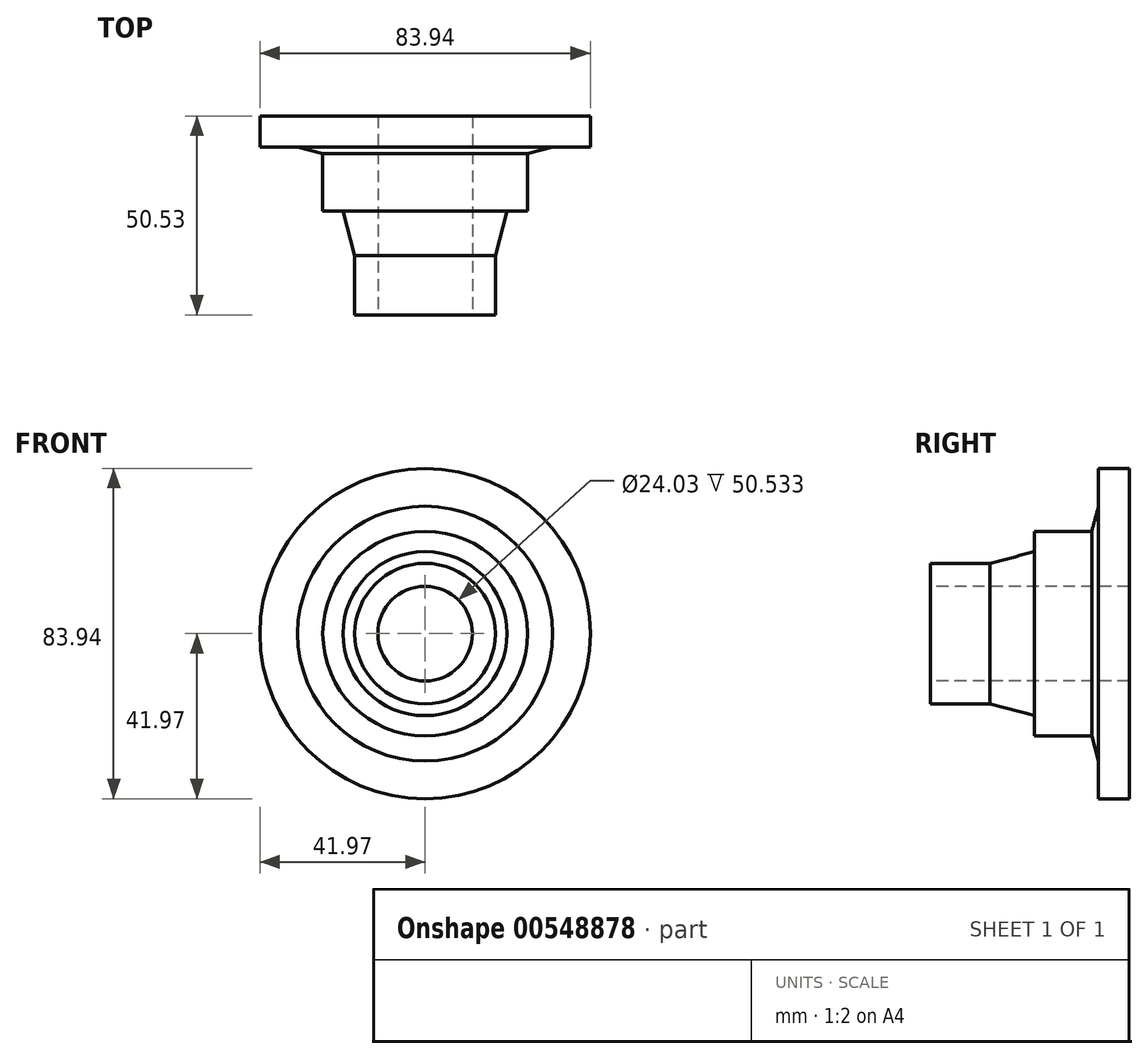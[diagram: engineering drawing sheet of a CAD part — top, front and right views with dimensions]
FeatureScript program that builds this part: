
annotation { "Feature Type Name" : "Feature", "Feature Type Description" : "" }
export const myFeature = defineFeature(function(context is Context, id is Id, definition is map)
    precondition{}
    {
        {
            var Q0;
            Q0=qCreatedBy(makeId("Right.planeOp"),FACE);
            var sketch = newSketch(context, id + "F0", { "sketchPlane" : qUnion([Q0])});
            skLineSegment(sketch, "E0", {"start": v(0, 0) * mm, "end": v(-50.53, 0) * mm});
            skLineSegment(sketch, "E1", {"start": v(-50.53, 0) * mm, "end": v(-50.53, 11.18) * mm});
            skLineSegment(sketch, "E2", {"start": v(-50.53, 11.18) * mm, "end": v(0, 11.18) * mm});
            skLineSegment(sketch, "E3", {"start": v(0, 11.18) * mm, "end": v(0, 0) * mm});
            skLineSegment(sketch, "E4", {"start": v(-50.53, 11.18) * mm, "end": v(-50.53, 17.86) * mm});
            skLineSegment(sketch, "E5", {"start": v(-50.53, 17.86) * mm, "end": v(-35.43, 17.86) * mm});
            skLineSegment(sketch, "E6", {"start": v(-35.43, 17.86) * mm, "end": v(-24.1, 20.84) * mm});
            skLineSegment(sketch, "E7", {"start": v(-24.1, 20.84) * mm, "end": v(-24.1, 26) * mm});
            skLineSegment(sketch, "E8", {"start": v(-24.1, 26) * mm, "end": v(-9.58, 26) * mm});
            skLineSegment(sketch, "E9", {"start": v(-9.58, 26) * mm, "end": v(-7.84, 32.38) * mm});
            skLineSegment(sketch, "E10", {"start": v(-7.84, 32.38) * mm, "end": v(-7.84, 41.97) * mm});
            skLineSegment(sketch, "E11", {"start": v(-7.84, 41.97) * mm, "end": v(0, 41.97) * mm});
            skLineSegment(sketch, "E12", {"start": v(0, 41.97) * mm, "end": v(0, 11.18) * mm});
            skSolve(sketch);
        }
        {
            var Q0;
            Q0=makeQuery(id+"F0.imprint","IMPRINT",FACE,{"disambiguationData":[TD([[makeQuery(id+"F0.imprint","IMPRINT",EDGE,{"derivedFrom":sQuery(id+"F0.wireOp",EDGE,"E2")}),1.0]])]});
            var Q1;
            Q1=makeQuery(id+"F0.imprint","IMPRINT",FACE,{"disambiguationData":[TD([[makeQuery(id+"F0.imprint","IMPRINT",EDGE,{"derivedFrom":sQuery(id+"F0.wireOp",EDGE,"E0")}),-1.0]])]});
            var Q2;
            Q2=sQuery(id+"F0.wireOp",EDGE,"E0");
            revolve(context, id + "F1", {"entities" : qUnion([Q0, Q1]), "axis" : qUnion([Q2]), "revolveType" : RevolveType.FULL});
        }
        {
            var Q0;
            Q0=makeQuery(id+"F1.opRevolve","SWEPT_FACE",FACE,{"disambiguationData":[OSD([sQuery(id+"F0.wireOp",EDGE,"E1"),sQuery(id+"F0.wireOp",EDGE,"E4")])]});
            var sketch = newSketch(context, id + "F2", { "sketchPlane" : qUnion([Q0])});
            skCircle(sketch, "E13", {"center": v(0, 0) * mm, "radius": 12.02 * mm});
            skSolve(sketch);
        }
        {
            var Q0;
            Q0=makeQuery(id+"F2.imprint","IMPRINT",FACE,{"disambiguationData":[TD([[makeQuery(id+"F2.imprint","IMPRINT",EDGE,{"derivedFrom":sQuery(id+"F2.wireOp",EDGE,"E13")}),1.0]])]});
            extrude(context, id + "F3", {"entities" : qUnion([Q0]), "operationType" : NewBodyOperationType.REMOVE, "endBound" : BoundingType.UP_TO_NEXT, "oppositeDirection" : true, "depth" : 25.4 * mm, "offsetDistance" : 25.4 * mm});
        }
    });
